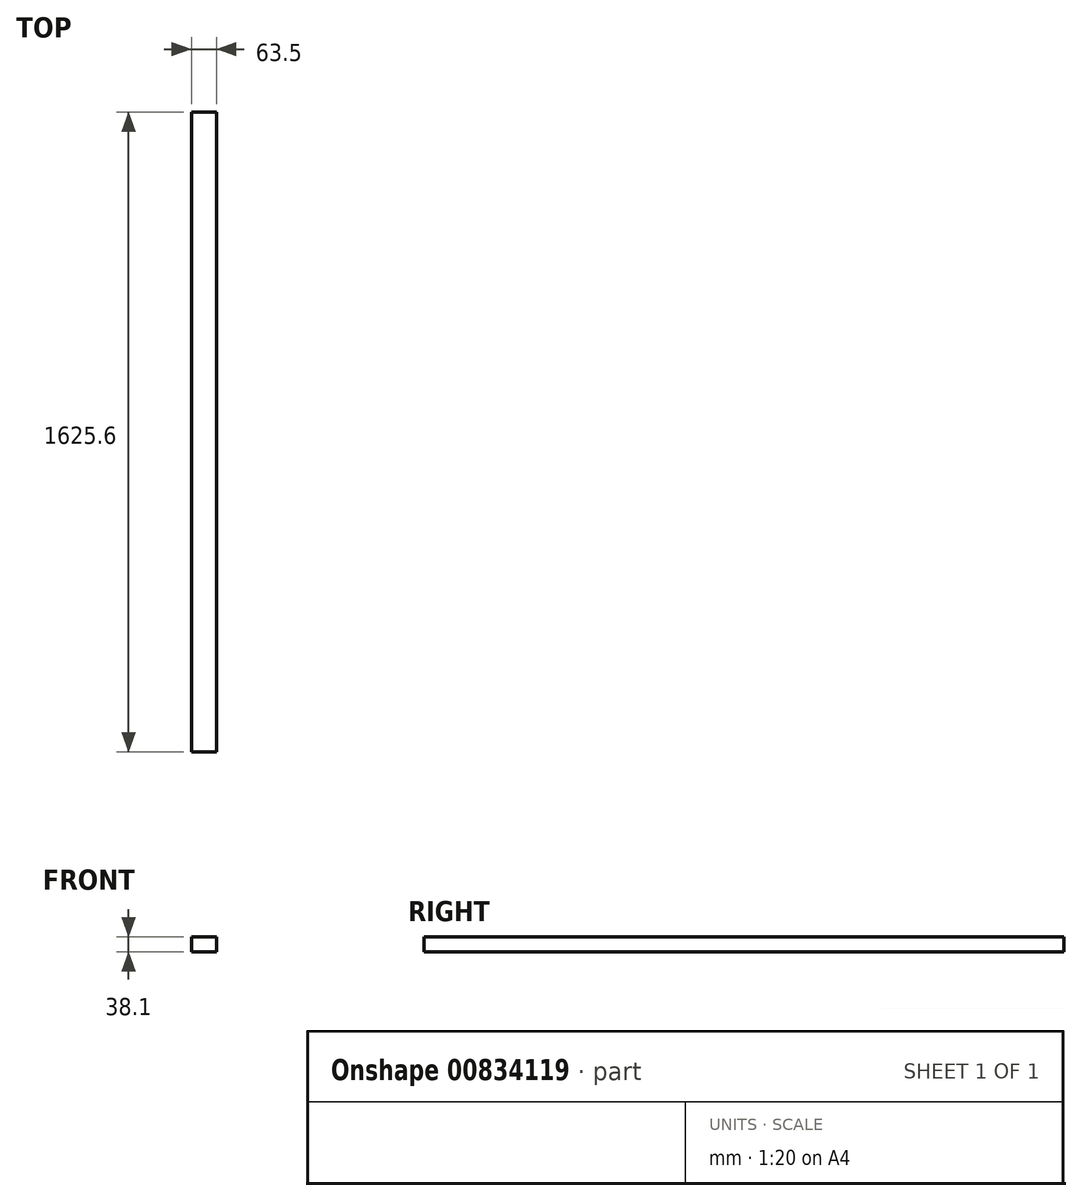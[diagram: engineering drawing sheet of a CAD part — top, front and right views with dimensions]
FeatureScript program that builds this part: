
annotation { "Feature Type Name" : "Feature", "Feature Type Description" : "" }
export const myFeature = defineFeature(function(context is Context, id is Id, definition is map)
    precondition{}
    {
        {
            var Q0;
            Q0=qCreatedBy(makeId("Front.planeOp"),FACE);
            var sketch = newSketch(context, id + "F0", { "sketchPlane" : qUnion([Q0])});
            skLineSegment(sketch, "E0.bottom", {"start": v(35.64, -16.66) * mm, "end": v(-27.86, -16.66) * mm});
            skLineSegment(sketch, "E0.top", {"start": v(35.64, 21.44) * mm, "end": v(-27.86, 21.44) * mm});
            skLineSegment(sketch, "E0.left", {"start": v(35.64, -16.66) * mm, "end": v(35.64, 21.44) * mm});
            skLineSegment(sketch, "E0.right", {"start": v(-27.86, -16.66) * mm, "end": v(-27.86, 21.44) * mm});
            skPoint(sketch, "E0.middle", {"position": v(3.9, 2.4) * mm});
            skSolve(sketch);
        }
        {
            var Q0;
            Q0=qSketchRegion(id+"F0",true);
            extrude(context, id + "F1", {"entities" : qUnion([Q0]), "depth" : 1625.6 * mm});
        }
    });
